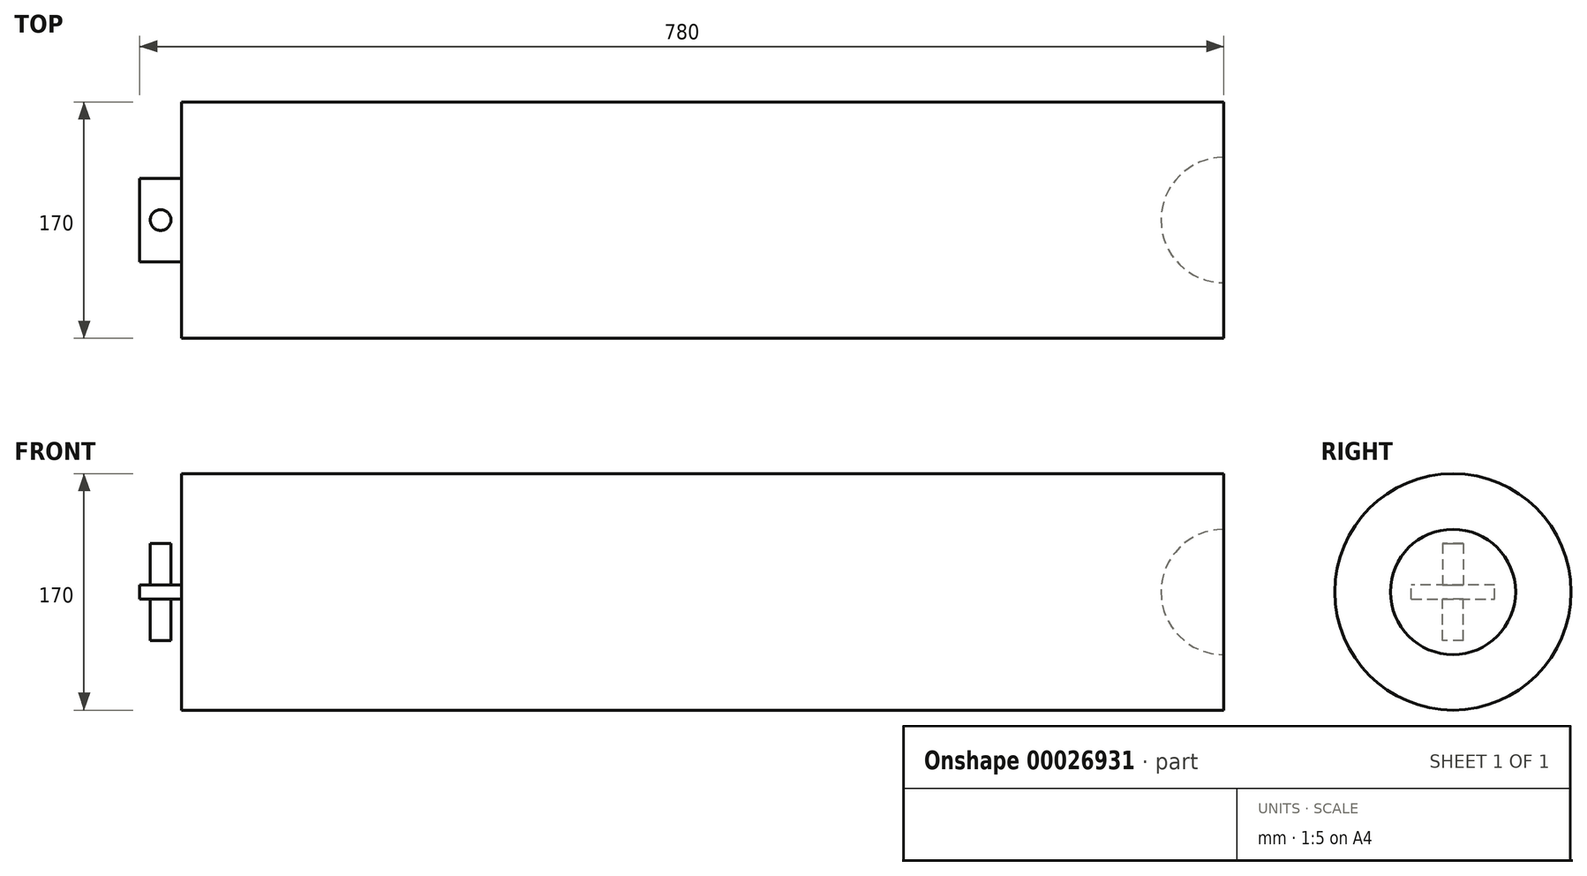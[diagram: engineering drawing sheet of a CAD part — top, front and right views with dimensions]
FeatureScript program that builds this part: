
annotation { "Feature Type Name" : "Feature", "Feature Type Description" : "" }
export const myFeature = defineFeature(function(context is Context, id is Id, definition is map)
    precondition{}
    {
        {
            var Q0;
            Q0=qCreatedBy(makeId("Front.planeOp"),FACE);
            var sketch = newSketch(context, id + "F0", { "sketchPlane" : qUnion([Q0])});
            skLineSegment(sketch, "E0", {"start": v(-72.31, -0.65) * mm, "end": v(677.69, -0.65) * mm});
            skLineSegment(sketch, "E1", {"start": v(-72.31, -0.65) * mm, "end": v(-72.31, 84.35) * mm});
            skLineSegment(sketch, "E2", {"start": v(-72.31, 84.35) * mm, "end": v(677.69, 84.35) * mm});
            skLineSegment(sketch, "E3", {"start": v(677.69, -0.65) * mm, "end": v(677.69, 84.35) * mm});
            skSolve(sketch);
        }
        {
            var Q0;
            Q0=makeQuery(id+"F0.imprint","IMPRINT",FACE,{"disambiguationData":[TD([[makeQuery(id+"F0.imprint","IMPRINT",EDGE,{"derivedFrom":sQuery(id+"F0.wireOp",EDGE,"E0")}),1.0]])]});
            var Q1;
            Q1=sQuery(id+"F0.wireOp",EDGE,"E0");
            revolve(context, id + "F1", {"entities" : qUnion([Q0]), "axis" : qUnion([Q1]), "revolveType" : RevolveType.FULL});
        }
        {
            var Q0;
            Q0=makeQuery(id+"F1.opRevolve","SWEPT_FACE",FACE,{"disambiguationData":[OSD([sQuery(id+"F0.wireOp",EDGE,"E1")])]});
            var sketch = newSketch(context, id + "F2", { "sketchPlane" : qUnion([Q0])});
            skLineSegment(sketch, "E4", {"start": v(-30, -0.65) * mm, "end": v(-30, 4.35) * mm});
            skLineSegment(sketch, "E5", {"start": v(30, -0.65) * mm, "end": v(30, 4.35) * mm});
            skLineSegment(sketch, "E6", {"start": v(0, 4.35) * mm, "end": v(-30, 4.35) * mm});
            skLineSegment(sketch, "E7", {"start": v(0, 4.35) * mm, "end": v(30, 4.35) * mm});
            skLineSegment(sketch, "E8", {"start": v(0, -5.65) * mm, "end": v(-30, -5.65) * mm});
            skLineSegment(sketch, "E9", {"start": v(-30, -5.65) * mm, "end": v(-30, -0.65) * mm});
            skLineSegment(sketch, "E10", {"start": v(0, -5.65) * mm, "end": v(30, -5.65) * mm});
            skLineSegment(sketch, "E11", {"start": v(30, -5.65) * mm, "end": v(30, -0.65) * mm});
            skSolve(sketch);
        }
        {
            var Q0;
            Q0=makeQuery(id+"F2.imprint","IMPRINT",FACE,{"disambiguationData":[TD([[makeQuery(id+"F2.imprint","IMPRINT",EDGE,{"derivedFrom":sQuery(id+"F2.wireOp",EDGE,"E4")}),-1.0]])]});
            extrude(context, id + "F3", {"entities" : qUnion([Q0]), "operationType" : NewBodyOperationType.ADD, "depth" : 30 * mm});
        }
        {
            var Q0;
            Q0=makeQuery(id+"F3.opExtrude","SWEPT_FACE",FACE,{"disambiguationData":[OSD([sQuery(id+"F2.wireOp",EDGE,"E6"),sQuery(id+"F2.wireOp",EDGE,"E7")])]});
            var sketch = newSketch(context, id + "F4", { "sketchPlane" : qUnion([Q0])});
            skCircle(sketch, "E12", {"center": v(-87.31, 0) * mm, "radius": 7.45 * mm});
            skPoint(sketch, "E13.orphan", {"position": v(-87.31, 30) * mm});
            skPoint(sketch, "E14.orphan", {"position": v(-102.31, 0) * mm});
            skSolve(sketch);
        }
        {
            var Q0;
            Q0=makeQuery(id+"F4.imprint","IMPRINT",FACE,{"disambiguationData":[TD([[makeQuery(id+"F4.imprint","IMPRINT",EDGE,{"derivedFrom":sQuery(id+"F4.wireOp",EDGE,"E12")}),1.0]])]});
            extrude(context, id + "F5", {"entities" : qUnion([Q0]), "operationType" : NewBodyOperationType.ADD, "depth" : 30 * mm});
        }
        {
            var Q0;
            Q0=makeQuery(id+"F3.opExtrude","SWEPT_FACE",FACE,{"disambiguationData":[OSD([sQuery(id+"F2.wireOp",EDGE,"E8"),sQuery(id+"F2.wireOp",EDGE,"E10")])]});
            var sketch = newSketch(context, id + "F6", { "sketchPlane" : qUnion([Q0])});
            skCircle(sketch, "E15", {"center": v(-87.31, 0) * mm, "radius": 7.45 * mm});
            skSolve(sketch);
        }
        {
            var Q0;
            Q0=makeQuery(id+"F6.imprint","IMPRINT",FACE,{"disambiguationData":[TD([[makeQuery(id+"F6.imprint","IMPRINT",EDGE,{"derivedFrom":sQuery(id+"F6.wireOp",EDGE,"E15")}),1.0]])]});
            extrude(context, id + "F7", {"entities" : qUnion([Q0]), "operationType" : NewBodyOperationType.ADD, "depth" : 30 * mm});
        }
        {
            var Q0;
            Q0=makeQuery(id+"F1.opRevolve","SWEPT_FACE",FACE,{"disambiguationData":[OSD([sQuery(id+"F0.wireOp",EDGE,"E3")])]});
            var sketch = newSketch(context, id + "F8", { "sketchPlane" : qUnion([Q0])});
            skLineSegment(sketch, "E16", {"start": v(0, 44.4) * mm, "end": v(0, -45.7) * mm});
            skArc(sketch, "E17", {"start": v(0, -45.7) * mm, "mid": v(45.05, -0.65) * mm, "end": v(0, 44.4) * mm});
            skSolve(sketch);
        }
        {
            var Q0;
            Q0=makeQuery(id+"F8.imprint","IMPRINT",FACE,{"disambiguationData":[TD([[makeQuery(id+"F8.imprint","IMPRINT",EDGE,{"derivedFrom":sQuery(id+"F8.wireOp",EDGE,"E16")}),1.0]])]});
            var Q1;
            Q1=sQuery(id+"F8.wireOp",EDGE,"E16");
            revolve(context, id + "F9", {"operationType" : NewBodyOperationType.REMOVE, "entities" : qUnion([Q0]), "axis" : qUnion([Q1]), "revolveType" : RevolveType.FULL, "oppositeDirection" : true});
        }
    });
